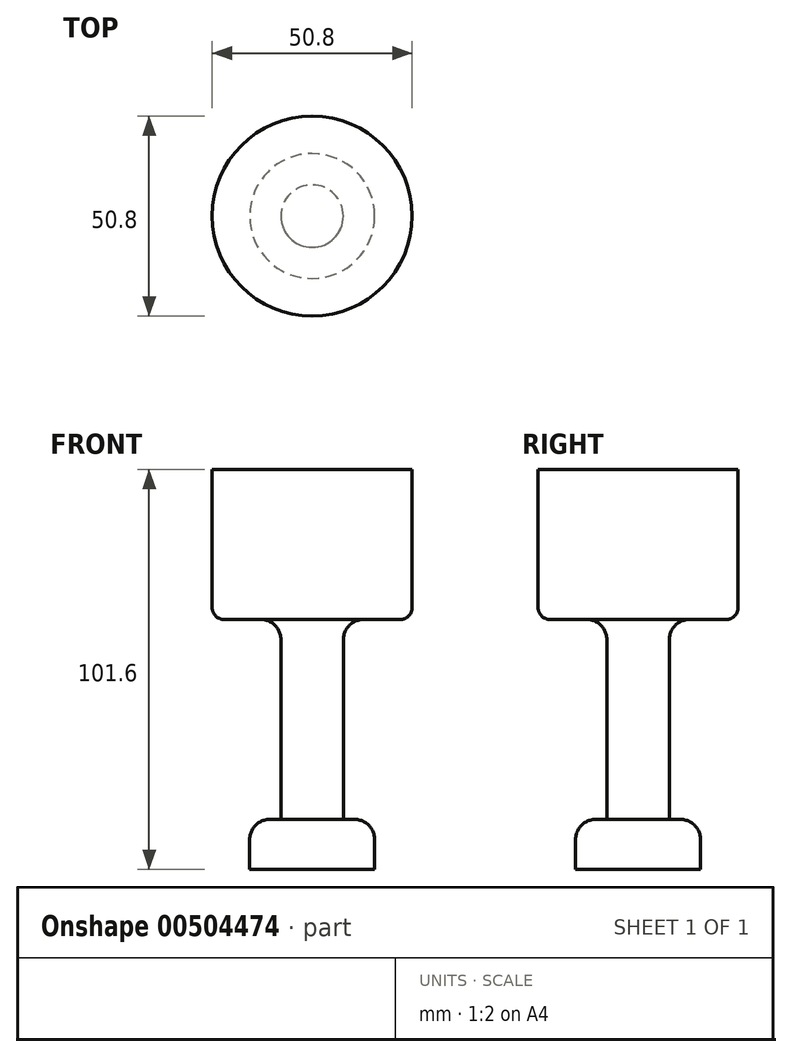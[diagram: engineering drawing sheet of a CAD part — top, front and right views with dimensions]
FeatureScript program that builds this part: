
annotation { "Feature Type Name" : "Feature", "Feature Type Description" : "" }
export const myFeature = defineFeature(function(context is Context, id is Id, definition is map)
    precondition{}
    {
        {
            var Q0;
            Q0=qCreatedBy(makeId("Front.planeOp"),FACE);
            var sketch = newSketch(context, id + "F0", { "sketchPlane" : qUnion([Q0])});
            skLineSegment(sketch, "E0", {"start": v(0, 67.47) * mm, "end": v(-25.4, 67.47) * mm});
            skLineSegment(sketch, "E1", {"start": v(-25.4, 67.47) * mm, "end": v(-25.4, 29.37) * mm});
            skLineSegment(sketch, "E2", {"start": v(-25.4, 29.37) * mm, "end": v(-7.94, 29.37) * mm});
            skLineSegment(sketch, "E3", {"start": v(-7.94, 29.37) * mm, "end": v(-7.94, -21.43) * mm});
            skLineSegment(sketch, "E4", {"start": v(-7.94, -21.43) * mm, "end": v(-15.87, -21.43) * mm});
            skLineSegment(sketch, "E5", {"start": v(-15.87, -21.43) * mm, "end": v(-15.87, -34.13) * mm});
            skLineSegment(sketch, "E6", {"start": v(-15.87, -34.13) * mm, "end": v(0, -34.13) * mm});
            skLineSegment(sketch, "E7", {"start": v(0, -34.13) * mm, "end": v(0, 67.47) * mm});
            skLineSegment(sketch, "E8", {"start": v(0, 73.15) * mm, "end": v(0, -54.49) * mm, "construction": true});
            skSolve(sketch);
        }
        {
            var Q0;
            Q0=makeQuery(id+"F0.imprint","IMPRINT",FACE,{"disambiguationData":[TD([[makeQuery(id+"F0.imprint","IMPRINT",EDGE,{"derivedFrom":sQuery(id+"F0.wireOp",EDGE,"E0")}),1.0]])]});
            var Q1;
            Q1=sQuery(id+"F0.wireOp",EDGE,"E8");
            revolve(context, id + "F1", {"entities" : qUnion([Q0]), "axis" : qUnion([Q1]), "revolveType" : RevolveType.FULL});
        }
        {
            var Q0;
            Q0=makeQuery(id+"F1.opRevolve","SWEPT_EDGE",EDGE,{"disambiguationData":[OSD([sQuery(id+"F0.wireOp",EDGE,"E2"),sQuery(id+"F0.wireOp",EDGE,"E3")])]});
            var Q1;
            Q1=makeQuery(id+"F1.opRevolve","SWEPT_EDGE",EDGE,{"disambiguationData":[OSD([sQuery(id+"F0.wireOp",EDGE,"E4"),sQuery(id+"F0.wireOp",EDGE,"E5")])]});
            fillet(context, id + "F2", {"entities" : qUnion([Q0, Q1]), "radius" : 5.08 * mm, "tangentPropagation" : true, "allowEdgeOverflow" : false});
        }
        {
            var Q0;
            Q0=makeQuery(id+"F1.opRevolve","SWEPT_EDGE",EDGE,{"disambiguationData":[OSD([sQuery(id+"F0.wireOp",EDGE,"E1"),sQuery(id+"F0.wireOp",EDGE,"E2")])]});
            fillet(context, id + "F3", {"entities" : qUnion([Q0]), "radius" : 3.05 * mm, "tangentPropagation" : true, "allowEdgeOverflow" : false});
        }
    });
